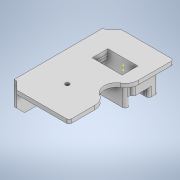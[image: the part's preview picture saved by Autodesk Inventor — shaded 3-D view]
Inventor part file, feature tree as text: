
AUTODESK INVENTOR PART (.ipt)
format: ipt  version: 2021 (Build 250183000, 183)  size: 290,304 bytes
history: native  units: mm
features: sketch x23, extrude x14, fillet x4, chamfer x2
ambient origin geometry x8: Origin, YZ Plane, XZ Plane, XY Plane, X Axis, Y Axis, Z Axis, Center Point
bodies: Body1 (feature_tree)
feature tree (43):
  extrude  "Extrusion3"  Depth=14.25mm TaperAngle=0.0deg
  sketch  "Sketch4"  dims[d7=35.0mm d8=12.0mm d9=0.0mm]
  extrude  "Extrusion4"  Depth=12.0mm TaperAngle=0.0deg
  sketch  "Sketch5"  dims[d10=15.0mm d11=4.0mm d12=0.0mm]
  sketch  "Sketch7"  dims[d35=80.0mm d36=3.0mm d37=0.0mm]
  extrude  "Extrusion5"  Depth=4.0mm TaperAngle=0.0deg
  sketch  "Sketch9"  dims[d41=5.0mm d42=0.0mm d43=7.0mm d44=0.0mm d45=2.0mm d46=2.0mm d47=6.0mm d48=2.0mm d49=45.0deg]
  sketch  "Sketch10"  dims[d50=3.0mm d51=23.2mm]
  extrude  "Extrusion9"  Depth=50.0mm
  extrude  "Extrusion10"  Depth=3.0mm TaperAngle=0.0deg
  extrude  "Extrusion11"  Depth=3.0mm TaperAngle=0.0deg
  extrude  "Extrusion12"  Depth=7.0mm TaperAngle=0.0deg
  fillet  "Fillet1"  Radius=2.0mm
  fillet  "Fillet2"  Radius=2.0mm
  sketch  "Sketch19"  dims[d69=2.0mm d70=10.0mm d71=0.0mm]
  chamfer  "Chamfer4"  Distance=6.0mm Angle=45.0deg
  sketch  "Sketch20"  dims[d72=10.0mm d75=10.0mm d76=0.0mm]
  extrude  "Extrusion13"  Depth=3.0mm
  sketch  "Sketch22"  dims[d78=2.0mm]
  sketch  "Sketch23"  dims[d79=10.0mm]
  extrude  "Extrusion14"  Depth=4.0mm TaperAngle=0.0deg
  chamfer  "Chamfer5"  Distance=2.0mm
  extrude  "Extrusion15"  Depth=2.0mm
  extrude  "Extrusion16"  Depth=4.0mm
  fillet  "Fillet3"  Radius=4.0mm
  extrude  "Extrusion17"  Depth=6.0mm
  fillet  "Fillet4"  Radius=2.152328mm
  extrude  "Extrusion18"  Depth=10.0mm TaperAngle=0.0deg
  extrude  "Extrusion19"  Depth=10.0mm TaperAngle=0.0deg
  sketch  "Sketch3"  dims[d4=2.0mm d5=14.25mm d6=0.0mm]
  sketch  "Sketch6"  dims[d33=11.005905mm d34=50.0mm]
  sketch  "Sketch8"  dims[d38=5.8mm d39=3.0mm d40=0.0mm]
  sketch  "Sketch15"  dims[d52=21.45mm d53=4.0mm d54=0.0mm d55=2.0mm d56=0.0mm]
  sketch  "Sketch16"  dims[d57=6.0mm d58=2.0mm d59=45.0deg d60=2.0mm]
  sketch  "Sketch17"  dims[d61=2.4mm d62=6.2mm d63=4.0mm d64=0.0mm]
  sketch  "Sketch18"  dims[d65=4.0mm d66=0.0mm d67=6.0mm d68=2.152328mm]
  sketch  "Sketch21"  dims[d77=2.0mm]
  sketch  "Sketch24"  dims[d80=24.0mm]
  sketch  "Sketch25"  dims[d81=10.0mm d82=0.0mm]
  sketch  "Sketch26"  dims[d26=0.5mm]
  sketch  "Sketch27"  dims[d27=0.872665mm]
  sketch  "Sketch28"  dims[d28=0.5mm]
  sketch  "Sketch29"  dims[d29=0.872665mm d30=0.5mm d31=0.872665mm d83=0.872665mm]
